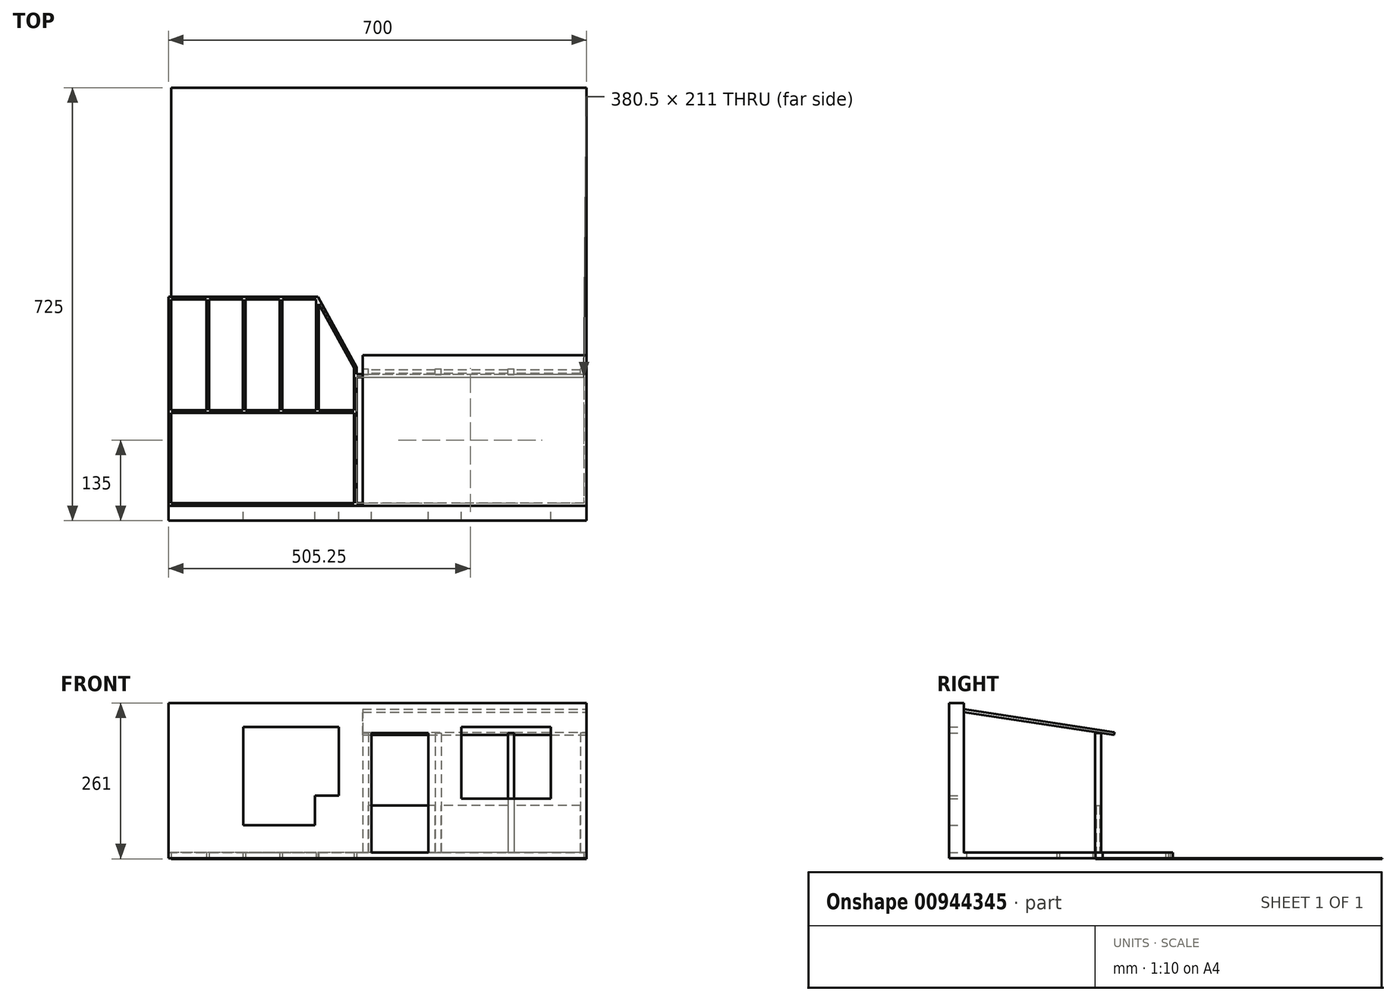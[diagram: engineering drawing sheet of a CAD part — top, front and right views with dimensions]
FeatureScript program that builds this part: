
annotation { "Feature Type Name" : "Feature", "Feature Type Description" : "" }
export const myFeature = defineFeature(function(context is Context, id is Id, definition is map)
    precondition{}
    {
        {
            var Q0;
            Q0=qCreatedBy(makeId("Top.planeOp"),FACE);
            var sketch = newSketch(context, id + "F0", { "sketchPlane" : qUnion([Q0])});
            skLineSegment(sketch, "E0", {"start": v(0, 0) * mm, "end": v(-385, 0) * mm});
            skLineSegment(sketch, "E1", {"start": v(-385, 0) * mm, "end": v(-700, 0) * mm});
            skLineSegment(sketch, "E2", {"start": v(-700, 0) * mm, "end": v(-700, 350) * mm});
            skLineSegment(sketch, "E3", {"start": v(-700, 350) * mm, "end": v(-450, 350) * mm});
            skLineSegment(sketch, "E4", {"start": v(-450, 350) * mm, "end": v(-385, 232) * mm});
            skLineSegment(sketch, "E5", {"start": v(-385, 232) * mm, "end": v(0, 232) * mm, "construction": true});
            skLineSegment(sketch, "E6", {"start": v(0, 232) * mm, "end": v(0, 0) * mm});
            skLineSegment(sketch, "E7", {"start": v(-385, 232) * mm, "end": v(-385, 0) * mm});
            skLineSegment(sketch, "E8", {"start": v(-385, 160) * mm, "end": v(-700, 160) * mm});
            skLineSegment(sketch, "E9", {"start": v(-385, 220) * mm, "end": v(0, 220) * mm});
            skLineSegment(sketch, "E10.0", {"start": v(-389.5, 230.84) * mm, "end": v(-389.5, 0) * mm});
            skLineSegment(sketch, "E10.1", {"start": v(-452.66, 345.5) * mm, "end": v(-389.5, 230.84) * mm});
            skLineSegment(sketch, "E10.2", {"start": v(-695.5, 345.5) * mm, "end": v(-452.66, 345.5) * mm});
            skLineSegment(sketch, "E10.3", {"start": v(-695.5, 0) * mm, "end": v(-695.5, 345.5) * mm});
            skLineSegment(sketch, "E11", {"start": v(-634.3, 160) * mm, "end": v(-634.3, 345.5) * mm, "construction": true});
            skLineSegment(sketch, "E12", {"start": v(-573.1, 160) * mm, "end": v(-573.1, 345.5) * mm, "construction": true});
            skLineSegment(sketch, "E13", {"start": v(-511.9, 160) * mm, "end": v(-511.9, 345.5) * mm, "construction": true});
            skLineSegment(sketch, "E14", {"start": v(-450.7, 160) * mm, "end": v(-450.7, 341.94) * mm, "construction": true});
            skLineSegment(sketch, "E15", {"start": v(-695.5, 257.02) * mm, "end": v(-634.3, 257.02) * mm, "construction": true});
            skLineSegment(sketch, "E16", {"start": v(-634.3, 257.02) * mm, "end": v(-573.1, 257.02) * mm, "construction": true});
            skLineSegment(sketch, "E17", {"start": v(-573.1, 257.02) * mm, "end": v(-511.9, 257.02) * mm, "construction": true});
            skLineSegment(sketch, "E18", {"start": v(-511.9, 257.02) * mm, "end": v(-450.7, 257.02) * mm, "construction": true});
            skLineSegment(sketch, "E19", {"start": v(-450.7, 190.59) * mm, "end": v(-389.5, 190.59) * mm, "construction": true});
            skLineSegment(sketch, "E20.0", {"start": v(-632.05, 160) * mm, "end": v(-632.05, 345.5) * mm});
            skLineSegment(sketch, "E21.0", {"start": v(-636.55, 160) * mm, "end": v(-636.55, 345.5) * mm});
            skLineSegment(sketch, "E22.0", {"start": v(-570.85, 160) * mm, "end": v(-570.85, 345.5) * mm});
            skLineSegment(sketch, "E23.0", {"start": v(-575.35, 160) * mm, "end": v(-575.35, 345.5) * mm});
            skLineSegment(sketch, "E24.0", {"start": v(-509.65, 160) * mm, "end": v(-509.65, 345.5) * mm});
            skLineSegment(sketch, "E25.0", {"start": v(-448.45, 160) * mm, "end": v(-448.45, 341.94) * mm});
            skLineSegment(sketch, "E26.0", {"start": v(-452.95, 160) * mm, "end": v(-452.95, 341.94) * mm});
            skLineSegment(sketch, "E27.0", {"start": v(-514.15, 160) * mm, "end": v(-514.15, 345.5) * mm});
            skLineSegment(sketch, "E28.0", {"start": v(-385, 4.5) * mm, "end": v(-700, 4.5) * mm});
            skLineSegment(sketch, "E28.1", {"start": v(-4.5, 4.5) * mm, "end": v(-385, 4.5) * mm});
            skLineSegment(sketch, "E28.2", {"start": v(-4.5, 232) * mm, "end": v(-4.5, 4.5) * mm});
            skLineSegment(sketch, "E29.0", {"start": v(-385, 215.5) * mm, "end": v(0, 215.5) * mm});
            skLineSegment(sketch, "E30.0", {"start": v(-385, 155.5) * mm, "end": v(-700, 155.5) * mm});
            skLineSegment(sketch, "E31", {"start": v(-452.95, 341.94) * mm, "end": v(-452.66, 347.98) * mm});
            skSolve(sketch);
        }
        {
            var Q0;
            {var subQ0=sQuery(id+"F0.wireOp",EDGE,"E2");var subQ1=sQuery(id+"F0.wireOp",EDGE,"E1");var subQ2=makeQuery(id+"F0.imprint","INTERSECT",VERTEX,{"derivedFrom":[subQ1,subQ0]});Q0=makeQuery(id+"F0.imprint","IMPRINT",FACE,{"disambiguationData":[TD([[makeQuery(id+"F0.imprint","IMPRINT",EDGE,{"disambiguationData":[TD([[subQ2,1.0]])],"derivedFrom":subQ1}),-1.0]])]});}
            var Q1;
            {var subQ0=sQuery(id+"F0.wireOp",EDGE,"E9");var subQ1=sQuery(id+"F0.wireOp",EDGE,"E6");var subQ2=makeQuery(id+"F0.imprint","INTERSECT",VERTEX,{"derivedFrom":[subQ1,subQ0]});Q1=makeQuery(id+"F0.imprint","IMPRINT",FACE,{"disambiguationData":[TD([[makeQuery(id+"F0.imprint","IMPRINT",EDGE,{"disambiguationData":[TD([[subQ2,-1.0]])],"derivedFrom":subQ1}),-1.0]])]});}
            var Q2;
            {var subQ1=sQuery(id+"F0.wireOp",EDGE,"E0");Q2=makeQuery(id+"F0.imprint","IMPRINT",FACE,{"disambiguationData":[TD([[makeQuery(id+"F0.imprint","IMPRINT",EDGE,{"derivedFrom":subQ1}),-1.0]])]});}
            var Q3;
            {var subQ1=sQuery(id+"F0.wireOp",EDGE,"E1");var subQ3=sQuery(id+"F0.wireOp",EDGE,"E10.0");var subQ4=makeQuery(id+"F0.imprint","INTERSECT",VERTEX,{"derivedFrom":[subQ1,subQ3]});Q3=makeQuery(id+"F0.imprint","IMPRINT",FACE,{"disambiguationData":[TD([[makeQuery(id+"F0.imprint","IMPRINT",EDGE,{"disambiguationData":[TD([[subQ4,1.0]])],"derivedFrom":subQ3}),1.0]])]});}
            var Q4;
            {var subQ0=sQuery(id+"F0.wireOp",EDGE,"E10.0");var subQ1=sQuery(id+"F0.wireOp",EDGE,"E1");var subQ2=makeQuery(id+"F0.imprint","INTERSECT",VERTEX,{"derivedFrom":[subQ1,subQ0]});Q4=makeQuery(id+"F0.imprint","IMPRINT",FACE,{"disambiguationData":[TD([[makeQuery(id+"F0.imprint","IMPRINT",EDGE,{"disambiguationData":[TD([[subQ2,-1.0]])],"derivedFrom":subQ1}),-1.0]])]});}
            var Q5;
            {var subQ0=sQuery(id+"F0.wireOp",EDGE,"E28.0");var subQ1=sQuery(id+"F0.wireOp",EDGE,"E2");var subQ2=makeQuery(id+"F0.imprint","INTERSECT",VERTEX,{"derivedFrom":[subQ1,subQ0]});Q5=makeQuery(id+"F0.imprint","IMPRINT",FACE,{"disambiguationData":[TD([[makeQuery(id+"F0.imprint","IMPRINT",EDGE,{"disambiguationData":[TD([[subQ2,-1.0]])],"derivedFrom":subQ1}),-1.0]])]});}
            var Q6;
            {var subQ0=sQuery(id+"F0.wireOp",EDGE,"E8");var subQ1=sQuery(id+"F0.wireOp",EDGE,"E2");var subQ2=makeQuery(id+"F0.imprint","INTERSECT",VERTEX,{"derivedFrom":[subQ1,subQ0]});Q6=makeQuery(id+"F0.imprint","IMPRINT",FACE,{"disambiguationData":[TD([[makeQuery(id+"F0.imprint","IMPRINT",EDGE,{"disambiguationData":[TD([[subQ2,1.0]])],"derivedFrom":subQ1}),-1.0]])]});}
            var Q7;
            {var subQ0=sQuery(id+"F0.wireOp",EDGE,"E9");var subQ1=sQuery(id+"F0.wireOp",EDGE,"E7");var subQ2=makeQuery(id+"F0.imprint","INTERSECT",VERTEX,{"derivedFrom":[subQ1,subQ0]});Q7=makeQuery(id+"F0.imprint","IMPRINT",FACE,{"disambiguationData":[TD([[makeQuery(id+"F0.imprint","IMPRINT",EDGE,{"disambiguationData":[TD([[subQ2,-1.0]])],"derivedFrom":subQ1}),1.0]])]});}
            var Q8;
            {var subQ9=sQuery(id+"F0.wireOp",EDGE,"E26.0");Q8=makeQuery(id+"F0.imprint","IMPRINT",FACE,{"disambiguationData":[TD([[makeQuery(id+"F0.imprint","IMPRINT",EDGE,{"derivedFrom":subQ9}),-1.0]])]});}
            var Q9;
            {var subQ21=sQuery(id+"F0.wireOp",EDGE,"E3");Q9=makeQuery(id+"F0.imprint","IMPRINT",FACE,{"disambiguationData":[TD([[makeQuery(id+"F0.imprint","IMPRINT",EDGE,{"derivedFrom":subQ21}),-1.0]])]});}
            var Q10;
            {var subQ0=sQuery(id+"F0.wireOp",EDGE,"E24.0");Q10=makeQuery(id+"F0.imprint","IMPRINT",FACE,{"disambiguationData":[TD([[makeQuery(id+"F0.imprint","IMPRINT",EDGE,{"derivedFrom":subQ0}),1.0]])]});}
            var Q11;
            {var subQ0=sQuery(id+"F0.wireOp",EDGE,"E22.0");Q11=makeQuery(id+"F0.imprint","IMPRINT",FACE,{"disambiguationData":[TD([[makeQuery(id+"F0.imprint","IMPRINT",EDGE,{"derivedFrom":subQ0}),1.0]])]});}
            var Q12;
            {var subQ0=sQuery(id+"F0.wireOp",EDGE,"E20.0");Q12=makeQuery(id+"F0.imprint","IMPRINT",FACE,{"disambiguationData":[TD([[makeQuery(id+"F0.imprint","IMPRINT",EDGE,{"derivedFrom":subQ0}),1.0]])]});}
            var Q13;
            {var subQ0=sQuery(id+"F0.wireOp",EDGE,"E8");var subQ10=makeQuery(id+"F0.imprint","INTERSECT",VERTEX,{"derivedFrom":[subQ0,sQuery(id+"F0.wireOp",EDGE,"E25.0")]});Q13=makeQuery(id+"F0.imprint","IMPRINT",FACE,{"disambiguationData":[TD([[makeQuery(id+"F0.imprint","IMPRINT",EDGE,{"disambiguationData":[TD([[subQ10,1.0]])],"derivedFrom":subQ0}),1.0]])]});}
            var Q14;
            {var subQ0=sQuery(id+"F0.wireOp",EDGE,"E8");var subQ1=sQuery(id+"F0.wireOp",EDGE,"E7");var subQ2=makeQuery(id+"F0.imprint","INTERSECT",VERTEX,{"derivedFrom":[subQ1,subQ0]});Q14=makeQuery(id+"F0.imprint","IMPRINT",FACE,{"disambiguationData":[TD([[makeQuery(id+"F0.imprint","IMPRINT",EDGE,{"disambiguationData":[TD([[subQ2,-1.0]])],"derivedFrom":subQ1}),-1.0]])]});}
            var Q15;
            {var subQ3=sQuery(id+"F0.wireOp",EDGE,"E30.0");var subQ5=sQuery(id+"F0.wireOp",EDGE,"E10.0");var subQ6=makeQuery(id+"F0.imprint","INTERSECT",VERTEX,{"derivedFrom":[subQ5,subQ3]});Q15=makeQuery(id+"F0.imprint","IMPRINT",FACE,{"disambiguationData":[TD([[makeQuery(id+"F0.imprint","IMPRINT",EDGE,{"disambiguationData":[TD([[subQ6,-1.0]])],"derivedFrom":subQ5}),1.0]])]});}
            extrude(context, id + "F1", {"entities" : qUnion([Q0, Q1, Q2, Q3, Q4, Q5, Q6, Q7, Q8, Q9, Q10, Q11, Q12, Q13, Q14, Q15]), "depth" : 9.5 * mm, "offsetDistance" : 25 * mm});
        }
        {
            var Q0;
            Q0=makeQuery(id+"F1.opExtrude","SWEPT_FACE",FACE,{"disambiguationData":[OSD([sQuery(id+"F0.wireOp",EDGE,"E0"),sQuery(id+"F0.wireOp",EDGE,"E1")])]});
            var sketch = newSketch(context, id + "F2", { "sketchPlane" : qUnion([Q0])});
            skLineSegment(sketch, "E32.bottom", {"start": v(0, 0) * mm, "end": v(-700, 0) * mm});
            skLineSegment(sketch, "E32.top", {"start": v(0, 260) * mm, "end": v(-700, 260) * mm});
            skLineSegment(sketch, "E32.left", {"start": v(0, 0) * mm, "end": v(0, 260) * mm});
            skLineSegment(sketch, "E32.right", {"start": v(-700, 0) * mm, "end": v(-700, 260) * mm});
            skLineSegment(sketch, "E33.bottom", {"start": v(-60, 99.5) * mm, "end": v(-210, 99.5) * mm});
            skLineSegment(sketch, "E33.top", {"start": v(-60, 219.5) * mm, "end": v(-210, 219.5) * mm});
            skLineSegment(sketch, "E33.left", {"start": v(-60, 99.5) * mm, "end": v(-60, 219.5) * mm});
            skLineSegment(sketch, "E33.right", {"start": v(-210, 99.5) * mm, "end": v(-210, 219.5) * mm});
            skLineSegment(sketch, "E34.bottom", {"start": v(-360, 9.5) * mm, "end": v(-265, 9.5) * mm});
            skLineSegment(sketch, "E34.top", {"start": v(-360, 209.5) * mm, "end": v(-265, 209.5) * mm});
            skLineSegment(sketch, "E34.left", {"start": v(-360, 9.5) * mm, "end": v(-360, 209.5) * mm});
            skLineSegment(sketch, "E34.right", {"start": v(-265, 9.5) * mm, "end": v(-265, 209.5) * mm});
            skLineSegment(sketch, "E35.bottom", {"start": v(-415, 220) * mm, "end": v(-455, 220) * mm});
            skLineSegment(sketch, "E35.top", {"start": v(-415, 105) * mm, "end": v(-455, 105) * mm});
            skLineSegment(sketch, "E35.left", {"start": v(-415, 220) * mm, "end": v(-415, 105) * mm});
            skLineSegment(sketch, "E35.right", {"start": v(-455, 220) * mm, "end": v(-455, 105) * mm});
            skLineSegment(sketch, "E36.bottom", {"start": v(-455, 220) * mm, "end": v(-575, 220) * mm});
            skLineSegment(sketch, "E36.top", {"start": v(-455, 55) * mm, "end": v(-575, 55) * mm});
            skLineSegment(sketch, "E36.left", {"start": v(-455, 220) * mm, "end": v(-455, 55) * mm});
            skLineSegment(sketch, "E36.right", {"start": v(-575, 220) * mm, "end": v(-575, 55) * mm});
            skSolve(sketch);
        }
        {
            var Q0;
            {var subQ1=sQuery(id+"F2.wireOp",EDGE,"E32.bottom");Q0=makeQuery(id+"F2.imprint","IMPRINT",FACE,{"disambiguationData":[TD([[makeQuery(id+"F2.imprint","IMPRINT",EDGE,{"derivedFrom":subQ1}),-1.0]])]});}
            var Q1;
            {var subQ1=sQuery(id+"F2.wireOp",EDGE,"E32.top");Q1=makeQuery(id+"F2.imprint","IMPRINT",FACE,{"disambiguationData":[TD([[makeQuery(id+"F2.imprint","IMPRINT",EDGE,{"derivedFrom":subQ1}),1.0]])]});}
            extrude(context, id + "F3", {"entities" : qUnion([Q0, Q1]), "operationType" : NewBodyOperationType.ADD, "depth" : 25 * mm, "offsetDistance" : 25 * mm});
        }
        {
            var Q0;
            Q0=makeQuery(id+"F3.boolean.opBoolean","MERGE",FACE,{"derivedFrom":[makeQuery(id+"F1.opExtrude","CAP_FACE",FACE,{"disambiguationData":[OSD([sQuery(id+"F0.wireOp",EDGE,"E0"),sQuery(id+"F0.wireOp",EDGE,"E1"),sQuery(id+"F0.wireOp",EDGE,"E2"),sQuery(id+"F0.wireOp",EDGE,"E3"),sQuery(id+"F0.wireOp",EDGE,"E4"),sQuery(id+"F0.wireOp",EDGE,"E6"),sQuery(id+"F0.wireOp",EDGE,"E7"),sQuery(id+"F0.wireOp",EDGE,"E8"),sQuery(id+"F0.wireOp",EDGE,"E9"),sQuery(id+"F0.wireOp",EDGE,"E10.0"),sQuery(id+"F0.wireOp",EDGE,"E10.1"),sQuery(id+"F0.wireOp",EDGE,"E10.2"),sQuery(id+"F0.wireOp",EDGE,"E10.3"),sQuery(id+"F0.wireOp",EDGE,"E20.0"),sQuery(id+"F0.wireOp",EDGE,"E21.0"),sQuery(id+"F0.wireOp",EDGE,"E22.0"),sQuery(id+"F0.wireOp",EDGE,"E23.0"),sQuery(id+"F0.wireOp",EDGE,"E24.0"),sQuery(id+"F0.wireOp",EDGE,"E25.0"),sQuery(id+"F0.wireOp",EDGE,"E26.0"),sQuery(id+"F0.wireOp",EDGE,"E27.0"),sQuery(id+"F0.wireOp",EDGE,"E28.0"),sQuery(id+"F0.wireOp",EDGE,"E28.1"),sQuery(id+"F0.wireOp",EDGE,"E28.2"),sQuery(id+"F0.wireOp",EDGE,"E29.0"),sQuery(id+"F0.wireOp",EDGE,"E30.0"),sQuery(id+"F0.wireOp",EDGE,"E31")])],"isStart":true}),makeQuery(id+"F3.opExtrude","SWEPT_FACE",FACE,{"disambiguationData":[OSD([sQuery(id+"F2.wireOp",EDGE,"E32.bottom")])]})]});
            var sketch = newSketch(context, id + "F4", { "sketchPlane" : qUnion([Q0])});
            skLineSegment(sketch, "E37.bottom", {"start": v(0, 0) * mm, "end": v(-695.5, 0) * mm});
            skLineSegment(sketch, "E37.top", {"start": v(0, -700) * mm, "end": v(-695.5, -700) * mm});
            skLineSegment(sketch, "E37.left", {"start": v(0, 0) * mm, "end": v(0, -700) * mm});
            skLineSegment(sketch, "E37.right", {"start": v(-695.5, 0) * mm, "end": v(-695.5, -700) * mm});
            skSolve(sketch);
        }
        {
            var Q0;
            {var subQ3=sQuery(id+"F4.wireOp",EDGE,"E37.top");Q0=makeQuery(id+"F4.imprint","IMPRINT",FACE,{"disambiguationData":[TD([[makeQuery(id+"F4.imprint","IMPRINT",EDGE,{"derivedFrom":subQ3}),-1.0]])]});}
            extrude(context, id + "F5", {"entities" : qUnion([Q0]), "operationType" : NewBodyOperationType.ADD, "depth" : 1 * mm, "offsetDistance" : 25 * mm});
        }
        {
            var Q0;
            Q0=makeQuery(id+"F3.boolean.opBoolean","MERGE",FACE,{"derivedFrom":[makeQuery(id+"F1.opExtrude","CAP_FACE",FACE,{"disambiguationData":[OSD([sQuery(id+"F0.wireOp",EDGE,"E0"),sQuery(id+"F0.wireOp",EDGE,"E1"),sQuery(id+"F0.wireOp",EDGE,"E2"),sQuery(id+"F0.wireOp",EDGE,"E3"),sQuery(id+"F0.wireOp",EDGE,"E4"),sQuery(id+"F0.wireOp",EDGE,"E6"),sQuery(id+"F0.wireOp",EDGE,"E7"),sQuery(id+"F0.wireOp",EDGE,"E8"),sQuery(id+"F0.wireOp",EDGE,"E9"),sQuery(id+"F0.wireOp",EDGE,"E10.0"),sQuery(id+"F0.wireOp",EDGE,"E10.1"),sQuery(id+"F0.wireOp",EDGE,"E10.2"),sQuery(id+"F0.wireOp",EDGE,"E10.3"),sQuery(id+"F0.wireOp",EDGE,"E20.0"),sQuery(id+"F0.wireOp",EDGE,"E21.0"),sQuery(id+"F0.wireOp",EDGE,"E22.0"),sQuery(id+"F0.wireOp",EDGE,"E23.0"),sQuery(id+"F0.wireOp",EDGE,"E24.0"),sQuery(id+"F0.wireOp",EDGE,"E25.0"),sQuery(id+"F0.wireOp",EDGE,"E26.0"),sQuery(id+"F0.wireOp",EDGE,"E27.0"),sQuery(id+"F0.wireOp",EDGE,"E28.0"),sQuery(id+"F0.wireOp",EDGE,"E28.1"),sQuery(id+"F0.wireOp",EDGE,"E28.2"),sQuery(id+"F0.wireOp",EDGE,"E29.0"),sQuery(id+"F0.wireOp",EDGE,"E30.0"),sQuery(id+"F0.wireOp",EDGE,"E31")])],"isStart":false}),makeQuery(id+"F3.opExtrude","SWEPT_FACE",FACE,{"disambiguationData":[OSD([sQuery(id+"F2.wireOp",EDGE,"E34.bottom")])]})]});
            var sketch = newSketch(context, id + "F6", { "sketchPlane" : qUnion([Q0])});
            skLineSegment(sketch, "E38.bottom", {"start": v(0, 0.5) * mm, "end": v(-700, 0.5) * mm});
            skLineSegment(sketch, "E38.top", {"start": v(0, 15) * mm, "end": v(-700, 15) * mm});
            skLineSegment(sketch, "E38.left", {"start": v(0, 0.5) * mm, "end": v(0, 15) * mm});
            skLineSegment(sketch, "E38.right", {"start": v(-700, 0.5) * mm, "end": v(-700, 15) * mm});
            skLineSegment(sketch, "E39.0.1.0", {"start": v(0, 29.6) * mm, "end": v(-700, 29.6) * mm});
            skLineSegment(sketch, "E39.0.1.1", {"start": v(0, 15.1) * mm, "end": v(-700, 15.1) * mm});
            skLineSegment(sketch, "E39.0.1.2", {"start": v(-700, 15.1) * mm, "end": v(-700, 29.6) * mm});
            skLineSegment(sketch, "E39.0.1.3", {"start": v(0, 15.1) * mm, "end": v(0, 29.6) * mm});
            skLineSegment(sketch, "E39.0.2.0", {"start": v(0, 44.2) * mm, "end": v(-700, 44.2) * mm});
            skLineSegment(sketch, "E39.0.2.1", {"start": v(0, 29.7) * mm, "end": v(-700, 29.7) * mm});
            skLineSegment(sketch, "E39.0.2.2", {"start": v(-700, 29.7) * mm, "end": v(-700, 44.2) * mm});
            skLineSegment(sketch, "E39.0.2.3", {"start": v(0, 29.7) * mm, "end": v(0, 44.2) * mm});
            skLineSegment(sketch, "E39.0.3.0", {"start": v(0, 58.8) * mm, "end": v(-700, 58.8) * mm});
            skLineSegment(sketch, "E39.0.3.1", {"start": v(0, 44.3) * mm, "end": v(-700, 44.3) * mm});
            skLineSegment(sketch, "E39.0.3.2", {"start": v(-700, 44.3) * mm, "end": v(-700, 58.8) * mm});
            skLineSegment(sketch, "E39.0.3.3", {"start": v(0, 44.3) * mm, "end": v(0, 58.8) * mm});
            skLineSegment(sketch, "E39.0.4.0", {"start": v(0, 73.4) * mm, "end": v(-700, 73.4) * mm});
            skLineSegment(sketch, "E39.0.4.1", {"start": v(0, 58.9) * mm, "end": v(-700, 58.9) * mm});
            skLineSegment(sketch, "E39.0.4.2", {"start": v(-700, 58.9) * mm, "end": v(-700, 73.4) * mm});
            skLineSegment(sketch, "E39.0.4.3", {"start": v(0, 58.9) * mm, "end": v(0, 73.4) * mm});
            skLineSegment(sketch, "E39.0.5.0", {"start": v(0, 88) * mm, "end": v(-700, 88) * mm});
            skLineSegment(sketch, "E39.0.5.1", {"start": v(0, 73.5) * mm, "end": v(-700, 73.5) * mm});
            skLineSegment(sketch, "E39.0.5.2", {"start": v(-700, 73.5) * mm, "end": v(-700, 88) * mm});
            skLineSegment(sketch, "E39.0.5.3", {"start": v(0, 73.5) * mm, "end": v(0, 88) * mm});
            skLineSegment(sketch, "E39.0.6.0", {"start": v(0, 102.6) * mm, "end": v(-700, 102.6) * mm});
            skLineSegment(sketch, "E39.0.6.1", {"start": v(0, 88.1) * mm, "end": v(-700, 88.1) * mm});
            skLineSegment(sketch, "E39.0.6.2", {"start": v(-700, 88.1) * mm, "end": v(-700, 102.6) * mm});
            skLineSegment(sketch, "E39.0.6.3", {"start": v(0, 88.1) * mm, "end": v(0, 102.6) * mm});
            skLineSegment(sketch, "E39.0.7.0", {"start": v(0, 117.2) * mm, "end": v(-700, 117.2) * mm});
            skLineSegment(sketch, "E39.0.7.1", {"start": v(0, 102.7) * mm, "end": v(-700, 102.7) * mm});
            skLineSegment(sketch, "E39.0.7.2", {"start": v(-700, 102.7) * mm, "end": v(-700, 117.2) * mm});
            skLineSegment(sketch, "E39.0.7.3", {"start": v(0, 102.7) * mm, "end": v(0, 117.2) * mm});
            skLineSegment(sketch, "E39.0.8.0", {"start": v(0, 131.8) * mm, "end": v(-700, 131.8) * mm});
            skLineSegment(sketch, "E39.0.8.1", {"start": v(0, 117.3) * mm, "end": v(-700, 117.3) * mm});
            skLineSegment(sketch, "E39.0.8.2", {"start": v(-700, 117.3) * mm, "end": v(-700, 131.8) * mm});
            skLineSegment(sketch, "E39.0.8.3", {"start": v(0, 117.3) * mm, "end": v(0, 131.8) * mm});
            skLineSegment(sketch, "E39.0.9.0", {"start": v(0, 146.4) * mm, "end": v(-700, 146.4) * mm});
            skLineSegment(sketch, "E39.0.9.1", {"start": v(0, 131.9) * mm, "end": v(-700, 131.9) * mm});
            skLineSegment(sketch, "E39.0.9.2", {"start": v(-700, 131.9) * mm, "end": v(-700, 146.4) * mm});
            skLineSegment(sketch, "E39.0.9.3", {"start": v(0, 131.9) * mm, "end": v(0, 146.4) * mm});
            skLineSegment(sketch, "E39.0.10.0", {"start": v(0, 161) * mm, "end": v(-700, 161) * mm});
            skLineSegment(sketch, "E39.0.10.1", {"start": v(0, 146.5) * mm, "end": v(-700, 146.5) * mm});
            skLineSegment(sketch, "E39.0.10.2", {"start": v(-700, 146.5) * mm, "end": v(-700, 161) * mm});
            skLineSegment(sketch, "E39.0.10.3", {"start": v(0, 146.5) * mm, "end": v(0, 161) * mm});
            skLineSegment(sketch, "E39.0.11.0", {"start": v(0, 175.6) * mm, "end": v(-700, 175.6) * mm});
            skLineSegment(sketch, "E39.0.11.1", {"start": v(0, 161.1) * mm, "end": v(-700, 161.1) * mm});
            skLineSegment(sketch, "E39.0.11.2", {"start": v(-700, 161.1) * mm, "end": v(-700, 175.6) * mm});
            skLineSegment(sketch, "E39.0.11.3", {"start": v(0, 161.1) * mm, "end": v(0, 175.6) * mm});
            skLineSegment(sketch, "E39.0.12.0", {"start": v(0, 190.2) * mm, "end": v(-700, 190.2) * mm});
            skLineSegment(sketch, "E39.0.12.1", {"start": v(0, 175.7) * mm, "end": v(-700, 175.7) * mm});
            skLineSegment(sketch, "E39.0.12.2", {"start": v(-700, 175.7) * mm, "end": v(-700, 190.2) * mm});
            skLineSegment(sketch, "E39.0.12.3", {"start": v(0, 175.7) * mm, "end": v(0, 190.2) * mm});
            skLineSegment(sketch, "E39.0.13.0", {"start": v(0, 204.8) * mm, "end": v(-700, 204.8) * mm});
            skLineSegment(sketch, "E39.0.13.1", {"start": v(0, 190.3) * mm, "end": v(-700, 190.3) * mm});
            skLineSegment(sketch, "E39.0.13.2", {"start": v(-700, 190.3) * mm, "end": v(-700, 204.8) * mm});
            skLineSegment(sketch, "E39.0.13.3", {"start": v(0, 190.3) * mm, "end": v(0, 204.8) * mm});
            skLineSegment(sketch, "E39.0.14.0", {"start": v(0, 219.4) * mm, "end": v(-700, 219.4) * mm});
            skLineSegment(sketch, "E39.0.14.1", {"start": v(0, 204.9) * mm, "end": v(-700, 204.9) * mm});
            skLineSegment(sketch, "E39.0.14.2", {"start": v(-700, 204.9) * mm, "end": v(-700, 219.4) * mm});
            skLineSegment(sketch, "E39.0.14.3", {"start": v(0, 204.9) * mm, "end": v(0, 219.4) * mm});
            skLineSegment(sketch, "E39.0.15.0", {"start": v(0, 234) * mm, "end": v(-700, 234) * mm});
            skLineSegment(sketch, "E39.0.15.1", {"start": v(0, 219.5) * mm, "end": v(-700, 219.5) * mm});
            skLineSegment(sketch, "E39.0.15.2", {"start": v(-700, 219.5) * mm, "end": v(-700, 234) * mm});
            skLineSegment(sketch, "E39.0.15.3", {"start": v(0, 219.5) * mm, "end": v(0, 234) * mm});
            skLineSegment(sketch, "E39.0.16.0", {"start": v(0, 248.6) * mm, "end": v(-700, 248.6) * mm});
            skLineSegment(sketch, "E39.0.16.1", {"start": v(0, 234.1) * mm, "end": v(-700, 234.1) * mm});
            skLineSegment(sketch, "E39.0.16.2", {"start": v(-700, 234.1) * mm, "end": v(-700, 248.6) * mm});
            skLineSegment(sketch, "E39.0.16.3", {"start": v(0, 234.1) * mm, "end": v(0, 248.6) * mm});
            skLineSegment(sketch, "E39.0.17.0", {"start": v(0, 263.2) * mm, "end": v(-700, 263.2) * mm});
            skLineSegment(sketch, "E39.0.17.1", {"start": v(0, 248.7) * mm, "end": v(-700, 248.7) * mm});
            skLineSegment(sketch, "E39.0.17.2", {"start": v(-700, 248.7) * mm, "end": v(-700, 263.2) * mm});
            skLineSegment(sketch, "E39.0.17.3", {"start": v(0, 248.7) * mm, "end": v(0, 263.2) * mm});
            skLineSegment(sketch, "E39.0.18.0", {"start": v(0, 277.8) * mm, "end": v(-700, 277.8) * mm});
            skLineSegment(sketch, "E39.0.18.1", {"start": v(0, 263.3) * mm, "end": v(-700, 263.3) * mm});
            skLineSegment(sketch, "E39.0.18.2", {"start": v(-700, 263.3) * mm, "end": v(-700, 277.8) * mm});
            skLineSegment(sketch, "E39.0.18.3", {"start": v(0, 263.3) * mm, "end": v(0, 277.8) * mm});
            skLineSegment(sketch, "E39.0.19.0", {"start": v(0, 292.4) * mm, "end": v(-700, 292.4) * mm});
            skLineSegment(sketch, "E39.0.19.1", {"start": v(0, 277.9) * mm, "end": v(-700, 277.9) * mm});
            skLineSegment(sketch, "E39.0.19.2", {"start": v(-700, 277.9) * mm, "end": v(-700, 292.4) * mm});
            skLineSegment(sketch, "E39.0.19.3", {"start": v(0, 277.9) * mm, "end": v(0, 292.4) * mm});
            skLineSegment(sketch, "E39.0.20.0", {"start": v(0, 307) * mm, "end": v(-700, 307) * mm});
            skLineSegment(sketch, "E39.0.20.1", {"start": v(0, 292.5) * mm, "end": v(-700, 292.5) * mm});
            skLineSegment(sketch, "E39.0.20.2", {"start": v(-700, 292.5) * mm, "end": v(-700, 307) * mm});
            skLineSegment(sketch, "E39.0.20.3", {"start": v(0, 292.5) * mm, "end": v(0, 307) * mm});
            skLineSegment(sketch, "E39.0.21.0", {"start": v(0, 321.6) * mm, "end": v(-700, 321.6) * mm});
            skLineSegment(sketch, "E39.0.21.1", {"start": v(0, 307.1) * mm, "end": v(-700, 307.1) * mm});
            skLineSegment(sketch, "E39.0.21.2", {"start": v(-700, 307.1) * mm, "end": v(-700, 321.6) * mm});
            skLineSegment(sketch, "E39.0.21.3", {"start": v(0, 307.1) * mm, "end": v(0, 321.6) * mm});
            skLineSegment(sketch, "E39.0.22.0", {"start": v(0, 336.2) * mm, "end": v(-700, 336.2) * mm});
            skLineSegment(sketch, "E39.0.22.1", {"start": v(0, 321.7) * mm, "end": v(-700, 321.7) * mm});
            skLineSegment(sketch, "E39.0.22.2", {"start": v(-700, 321.7) * mm, "end": v(-700, 336.2) * mm});
            skLineSegment(sketch, "E39.0.22.3", {"start": v(0, 321.7) * mm, "end": v(0, 336.2) * mm});
            skLineSegment(sketch, "E39.direction1", {"start": v(-700, 15) * mm, "end": v(-675, 15) * mm, "construction": true});
            skLineSegment(sketch, "E39.direction2", {"start": v(-700, 15) * mm, "end": v(-700, 29.6) * mm, "construction": true});
            skLineSegment(sketch, "E40.0.0.23", {"start": v(0, 350.8) * mm, "end": v(-700, 350.8) * mm});
            skLineSegment(sketch, "E40.3.0.23", {"start": v(0, 336.3) * mm, "end": v(-700, 336.3) * mm});
            skLineSegment(sketch, "E40.6.0.23", {"start": v(-700, 336.3) * mm, "end": v(-700, 350.8) * mm});
            skLineSegment(sketch, "E40.9.0.23", {"start": v(0, 336.3) * mm, "end": v(0, 350.8) * mm});
            skSolve(sketch);
        }
        {
            var Q0;
            Q0=makeQuery(id+"F5.opExtrude","CAP_FACE",FACE,{"disambiguationData":[OSD([sQuery(id+"F0.wireOp",EDGE,"E3"),sQuery(id+"F0.wireOp",EDGE,"E4"),sQuery(id+"F0.wireOp",EDGE,"E7"),sQuery(id+"F0.wireOp",EDGE,"E9"),sQuery(id+"F4.wireOp",EDGE,"E37.top"),sQuery(id+"F4.wireOp",EDGE,"E37.left"),sQuery(id+"F4.wireOp",EDGE,"E37.right")])],"isStart":true});
            var sketch = newSketch(context, id + "F7", { "sketchPlane" : qUnion([Q0])});
            skLineSegment(sketch, "E41.0.0", {"start": v(-450, 350) * mm, "end": v(-695.5, 350) * mm});
            skLineSegment(sketch, "E41.0.1", {"start": v(-695.5, 350) * mm, "end": v(-695.5, 700) * mm});
            skLineSegment(sketch, "E41.0.2", {"start": v(-695.5, 700) * mm, "end": v(0, 700) * mm});
            skLineSegment(sketch, "E41.0.3", {"start": v(0, 700) * mm, "end": v(0, 220) * mm});
            skLineSegment(sketch, "E41.0.4", {"start": v(0, 220) * mm, "end": v(-385, 220) * mm});
            skLineSegment(sketch, "E41.0.5", {"start": v(-385, 220) * mm, "end": v(-385, 232) * mm});
            skLineSegment(sketch, "E41.0.6", {"start": v(-385, 232) * mm, "end": v(-450, 350) * mm});
            skSolve(sketch);
        }
        {
            var Q0;
            Q0 = qSketchRegion(id + "F7", true);
            extrude(context, id + "F8", {"entities" : qUnion([Q0]), "operationType" : NewBodyOperationType.REMOVE, "endBound" : BoundingType.THROUGH_ALL, "depth" : 25 * mm, "offsetDistance" : 25 * mm});
        }
        {
            var Q0;
            {var subQ0=sQuery(id+"F0.wireOp",EDGE,"E6");var subQ1=sQuery(id+"F0.wireOp",EDGE,"E28.2");var subQ2=sQuery(id+"F6.wireOp",EDGE,"E39.0.14.1");var subQ3=sQuery(id+"F6.wireOp",EDGE,"E39.0.13.0");var subQ4=sQuery(id+"F6.wireOp",EDGE,"E39.0.13.3");var subQ5=sQuery(id+"F6.wireOp",EDGE,"E39.0.14.3");Q0=makeQuery(id+"FQyzF96Mlg0WZgH_2.boolean.opBoolean","SPLIT",FACE,{"disambiguationData":[TD([makeQuery(id+"F1.opExtrude","SWEPT_FACE",FACE,{"disambiguationData":[OSD([subQ0])]}),makeQuery(id+"F1.opExtrude","SWEPT_FACE",FACE,{"disambiguationData":[OSD([subQ1])]}),makeQuery(id+"F3.opExtrude","SWEPT_FACE",FACE,{"disambiguationData":[OSD([sQuery(id+"F2.wireOp",EDGE,"E32.left")])]}),makeQuery(id+"FQyzF96Mlg0WZgH_2.opExtrude","SWEPT_FACE",FACE,{"disambiguationData":[OSD([sQuery(id+"F6.wireOp",EDGE,"E38.left")])]}),makeQuery(id+"FQyzF96Mlg0WZgH_2.opExtrude","SWEPT_FACE",FACE,{"disambiguationData":[OSD([sQuery(id+"F6.wireOp",EDGE,"E39.0.1.3")])]}),makeQuery(id+"FQyzF96Mlg0WZgH_2.opExtrude","SWEPT_FACE",FACE,{"disambiguationData":[OSD([sQuery(id+"F6.wireOp",EDGE,"E39.0.2.3")])]}),makeQuery(id+"FQyzF96Mlg0WZgH_2.opExtrude","SWEPT_FACE",FACE,{"disambiguationData":[OSD([sQuery(id+"F6.wireOp",EDGE,"E39.0.3.3")])]}),makeQuery(id+"FQyzF96Mlg0WZgH_2.opExtrude","SWEPT_FACE",FACE,{"disambiguationData":[OSD([sQuery(id+"F6.wireOp",EDGE,"E39.0.4.3")])]}),makeQuery(id+"FQyzF96Mlg0WZgH_2.opExtrude","SWEPT_FACE",FACE,{"disambiguationData":[OSD([sQuery(id+"F6.wireOp",EDGE,"E39.0.5.3")])]}),makeQuery(id+"FQyzF96Mlg0WZgH_2.opExtrude","SWEPT_FACE",FACE,{"disambiguationData":[OSD([sQuery(id+"F6.wireOp",EDGE,"E39.0.6.3")])]}),makeQuery(id+"FQyzF96Mlg0WZgH_2.opExtrude","SWEPT_FACE",FACE,{"disambiguationData":[OSD([sQuery(id+"F6.wireOp",EDGE,"E39.0.7.3")])]}),makeQuery(id+"FQyzF96Mlg0WZgH_2.opExtrude","SWEPT_FACE",FACE,{"disambiguationData":[OSD([sQuery(id+"F6.wireOp",EDGE,"E39.0.8.3")])]}),makeQuery(id+"FQyzF96Mlg0WZgH_2.opExtrude","SWEPT_FACE",FACE,{"disambiguationData":[OSD([sQuery(id+"F6.wireOp",EDGE,"E39.0.9.3")])]}),makeQuery(id+"FQyzF96Mlg0WZgH_2.opExtrude","SWEPT_FACE",FACE,{"disambiguationData":[OSD([sQuery(id+"F6.wireOp",EDGE,"E39.0.10.3")])]}),makeQuery(id+"FQyzF96Mlg0WZgH_2.opExtrude","SWEPT_FACE",FACE,{"disambiguationData":[OSD([sQuery(id+"F6.wireOp",EDGE,"E39.0.11.3")])]}),makeQuery(id+"FQyzF96Mlg0WZgH_2.opExtrude","SWEPT_FACE",FACE,{"disambiguationData":[OSD([sQuery(id+"F6.wireOp",EDGE,"E39.0.12.3")])]}),makeQuery(id+"FQyzF96Mlg0WZgH_2.opExtrude","SWEPT_FACE",FACE,{"disambiguationData":[OSD([subQ3])]}),makeQuery(id+"FQyzF96Mlg0WZgH_2.opExtrude","CAP_FACE",FACE,{"disambiguationData":[OSD([subQ3,sQuery(id+"F6.wireOp",EDGE,"E39.0.13.1"),sQuery(id+"F6.wireOp",EDGE,"E39.0.13.2"),subQ4])],"isStart":true}),makeQuery(id+"FQyzF96Mlg0WZgH_2.opExtrude","SWEPT_FACE",FACE,{"disambiguationData":[OSD([subQ4])]}),makeQuery(id+"FQyzF96Mlg0WZgH_2.opExtrude","CAP_FACE",FACE,{"disambiguationData":[OSD([sQuery(id+"F6.wireOp",EDGE,"E39.0.14.0"),subQ2,sQuery(id+"F6.wireOp",EDGE,"E39.0.14.2"),subQ5])],"isStart":true}),makeQuery(id+"FQyzF96Mlg0WZgH_2.opExtrude","SWEPT_FACE",FACE,{"disambiguationData":[OSD([subQ2])]}),makeQuery(id+"FQyzF96Mlg0WZgH_2.opExtrude","SWEPT_FACE",FACE,{"disambiguationData":[OSD([subQ5])]})])],"derivedFrom":makeQuery(id+"F3.boolean.opBoolean","MERGE",FACE,{"derivedFrom":[makeQuery(id+"F1.opExtrude","CAP_FACE",FACE,{"disambiguationData":[OSD([sQuery(id+"F0.wireOp",EDGE,"E0"),sQuery(id+"F0.wireOp",EDGE,"E1"),sQuery(id+"F0.wireOp",EDGE,"E2"),sQuery(id+"F0.wireOp",EDGE,"E3"),sQuery(id+"F0.wireOp",EDGE,"E4"),subQ0,sQuery(id+"F0.wireOp",EDGE,"E7"),sQuery(id+"F0.wireOp",EDGE,"E8"),sQuery(id+"F0.wireOp",EDGE,"E9"),sQuery(id+"F0.wireOp",EDGE,"E10.0"),sQuery(id+"F0.wireOp",EDGE,"E10.1"),sQuery(id+"F0.wireOp",EDGE,"E10.2"),sQuery(id+"F0.wireOp",EDGE,"E10.3"),sQuery(id+"F0.wireOp",EDGE,"E20.0"),sQuery(id+"F0.wireOp",EDGE,"E21.0"),sQuery(id+"F0.wireOp",EDGE,"E22.0"),sQuery(id+"F0.wireOp",EDGE,"E23.0"),sQuery(id+"F0.wireOp",EDGE,"E24.0"),sQuery(id+"F0.wireOp",EDGE,"E25.0"),sQuery(id+"F0.wireOp",EDGE,"E26.0"),sQuery(id+"F0.wireOp",EDGE,"E27.0"),sQuery(id+"F0.wireOp",EDGE,"E28.0"),sQuery(id+"F0.wireOp",EDGE,"E28.1"),subQ1,sQuery(id+"F0.wireOp",EDGE,"E29.0"),sQuery(id+"F0.wireOp",EDGE,"E30.0"),sQuery(id+"F0.wireOp",EDGE,"E31")])],"isStart":false}),makeQuery(id+"F3.opExtrude","SWEPT_FACE",FACE,{"disambiguationData":[OSD([sQuery(id+"F2.wireOp",EDGE,"E34.bottom")])]})]})});}
            var sketch = newSketch(context, id + "F9", { "sketchPlane" : qUnion([Q0])});
            skLineSegment(sketch, "E42.bottom", {"start": v(0, 219.49) * mm, "end": v(-10, 219.49) * mm});
            skLineSegment(sketch, "E42.top", {"start": v(0, 229.49) * mm, "end": v(-10, 229.49) * mm});
            skLineSegment(sketch, "E42.left", {"start": v(0, 219.49) * mm, "end": v(0, 229.49) * mm});
            skLineSegment(sketch, "E42.right", {"start": v(-10, 219.49) * mm, "end": v(-10, 229.49) * mm});
            skLineSegment(sketch, "E43.bottom", {"start": v(-375, 219.49) * mm, "end": v(-365, 219.49) * mm});
            skLineSegment(sketch, "E43.top", {"start": v(-375, 229.49) * mm, "end": v(-365, 229.49) * mm});
            skLineSegment(sketch, "E43.left", {"start": v(-375, 219.49) * mm, "end": v(-375, 229.49) * mm});
            skLineSegment(sketch, "E43.right", {"start": v(-365, 219.49) * mm, "end": v(-365, 229.49) * mm});
            skLineSegment(sketch, "E44.bottom", {"start": v(-253.33, 219.49) * mm, "end": v(-243.33, 219.49) * mm});
            skLineSegment(sketch, "E44.top", {"start": v(-253.33, 229.49) * mm, "end": v(-243.33, 229.49) * mm});
            skLineSegment(sketch, "E44.left", {"start": v(-253.33, 219.49) * mm, "end": v(-253.33, 229.49) * mm});
            skLineSegment(sketch, "E44.right", {"start": v(-243.33, 219.49) * mm, "end": v(-243.33, 229.49) * mm});
            skLineSegment(sketch, "E45.bottom", {"start": v(-131.67, 219.49) * mm, "end": v(-121.67, 219.49) * mm});
            skLineSegment(sketch, "E45.top", {"start": v(-131.67, 229.49) * mm, "end": v(-121.67, 229.49) * mm});
            skLineSegment(sketch, "E45.left", {"start": v(-131.67, 219.49) * mm, "end": v(-131.67, 229.49) * mm});
            skLineSegment(sketch, "E45.right", {"start": v(-121.67, 219.49) * mm, "end": v(-121.67, 229.49) * mm});
            skLineSegment(sketch, "E46", {"start": v(-10, 229.49) * mm, "end": v(-121.67, 229.49) * mm, "construction": true});
            skLineSegment(sketch, "E47", {"start": v(-131.67, 229.49) * mm, "end": v(-243.33, 229.49) * mm, "construction": true});
            skLineSegment(sketch, "E48", {"start": v(-253.33, 229.49) * mm, "end": v(-365, 229.49) * mm, "construction": true});
            skSolve(sketch);
        }
        {
            var Q0;
            Q0 = qSketchRegion(id + "F9", true);
            extrude(context, id + "F10", {"entities" : qUnion([Q0]), "operationType" : NewBodyOperationType.ADD, "depth" : 200 * mm, "offsetDistance" : 25 * mm});
        }
        {
            var Q0;
            Q0=makeQuery(id+"F10.boolean.opBoolean","MERGE",FACE,{"derivedFrom":[makeQuery(id+"FQyzF96Mlg0WZgH_2.boolean.opBoolean","MERGE",FACE,{"derivedFrom":[makeQuery(id+"F3.boolean.opBoolean","MERGE",FACE,{"derivedFrom":[makeQuery(id+"F1.opExtrude","SWEPT_FACE",FACE,{"disambiguationData":[OSD([sQuery(id+"F0.wireOp",EDGE,"E6")])]}),makeQuery(id+"F3.opExtrude","SWEPT_FACE",FACE,{"disambiguationData":[OSD([sQuery(id+"F2.wireOp",EDGE,"E32.left")])]})]}),makeQuery(id+"FQyzF96Mlg0WZgH_2.opExtrude","SWEPT_FACE",FACE,{"disambiguationData":[OSD([sQuery(id+"F6.wireOp",EDGE,"E38.left")])]}),makeQuery(id+"FQyzF96Mlg0WZgH_2.opExtrude","SWEPT_FACE",FACE,{"disambiguationData":[OSD([sQuery(id+"F6.wireOp",EDGE,"E39.0.1.3")])]}),makeQuery(id+"FQyzF96Mlg0WZgH_2.opExtrude","SWEPT_FACE",FACE,{"disambiguationData":[OSD([sQuery(id+"F6.wireOp",EDGE,"E39.0.2.3")])]}),makeQuery(id+"FQyzF96Mlg0WZgH_2.opExtrude","SWEPT_FACE",FACE,{"disambiguationData":[OSD([sQuery(id+"F6.wireOp",EDGE,"E39.0.3.3")])]}),makeQuery(id+"FQyzF96Mlg0WZgH_2.opExtrude","SWEPT_FACE",FACE,{"disambiguationData":[OSD([sQuery(id+"F6.wireOp",EDGE,"E39.0.4.3")])]}),makeQuery(id+"FQyzF96Mlg0WZgH_2.opExtrude","SWEPT_FACE",FACE,{"disambiguationData":[OSD([sQuery(id+"F6.wireOp",EDGE,"E39.0.5.3")])]}),makeQuery(id+"FQyzF96Mlg0WZgH_2.opExtrude","SWEPT_FACE",FACE,{"disambiguationData":[OSD([sQuery(id+"F6.wireOp",EDGE,"E39.0.6.3")])]}),makeQuery(id+"FQyzF96Mlg0WZgH_2.opExtrude","SWEPT_FACE",FACE,{"disambiguationData":[OSD([sQuery(id+"F6.wireOp",EDGE,"E39.0.7.3")])]}),makeQuery(id+"FQyzF96Mlg0WZgH_2.opExtrude","SWEPT_FACE",FACE,{"disambiguationData":[OSD([sQuery(id+"F6.wireOp",EDGE,"E39.0.8.3")])]}),makeQuery(id+"FQyzF96Mlg0WZgH_2.opExtrude","SWEPT_FACE",FACE,{"disambiguationData":[OSD([sQuery(id+"F6.wireOp",EDGE,"E39.0.9.3")])]}),makeQuery(id+"FQyzF96Mlg0WZgH_2.opExtrude","SWEPT_FACE",FACE,{"disambiguationData":[OSD([sQuery(id+"F6.wireOp",EDGE,"E39.0.10.3")])]}),makeQuery(id+"FQyzF96Mlg0WZgH_2.opExtrude","SWEPT_FACE",FACE,{"disambiguationData":[OSD([sQuery(id+"F6.wireOp",EDGE,"E39.0.11.3")])]}),makeQuery(id+"FQyzF96Mlg0WZgH_2.opExtrude","SWEPT_FACE",FACE,{"disambiguationData":[OSD([sQuery(id+"F6.wireOp",EDGE,"E39.0.12.3")])]}),makeQuery(id+"FQyzF96Mlg0WZgH_2.opExtrude","SWEPT_FACE",FACE,{"disambiguationData":[OSD([sQuery(id+"F6.wireOp",EDGE,"E39.0.13.3")])]}),makeQuery(id+"FQyzF96Mlg0WZgH_2.opExtrude","SWEPT_FACE",FACE,{"disambiguationData":[OSD([sQuery(id+"F6.wireOp",EDGE,"E39.0.14.3")])]})]}),makeQuery(id+"F10.opExtrude","SWEPT_FACE",FACE,{"disambiguationData":[OSD([sQuery(id+"F9.wireOp",EDGE,"E42.left")])]})]});
            var sketch = newSketch(context, id + "F11", { "sketchPlane" : qUnion([Q0])});
            skLineSegment(sketch, "E49", {"start": v(252.06, 211.12) * mm, "end": v(251.3, 206.17) * mm});
            skLineSegment(sketch, "E50", {"start": v(251.3, 206.17) * mm, "end": v(0, 244.5) * mm});
            skLineSegment(sketch, "E51", {"start": v(0, 244.5) * mm, "end": v(0, 249.56) * mm});
            skLineSegment(sketch, "E52", {"start": v(0, 249.56) * mm, "end": v(252.06, 211.12) * mm});
            skSolve(sketch);
        }
        {
            var Q0;
            {var subQ4=sQuery(id+"F11.wireOp",EDGE,"E49");Q0=makeQuery(id+"F11.imprint","IMPRINT",FACE,{"disambiguationData":[TD([[makeQuery(id+"F11.imprint","IMPRINT",EDGE,{"derivedFrom":subQ4}),-1.0]])]});}
            var Q1;
            Q1=makeQuery(id+"F10.opExtrude","SWEPT_FACE",FACE,{"disambiguationData":[OSD([sQuery(id+"F9.wireOp",EDGE,"E43.left")])]});
            extrude(context, id + "F12", {"entities" : qUnion([Q0]), "endBound" : BoundingType.UP_TO_SURFACE, "oppositeDirection" : true, "depth" : 25 * mm, "endBoundEntityFace" : qUnion([Q1]), "offsetDistance" : 25 * mm});
        }
        {
            var Q0;
            Q0=makeQuery(id+"F10.opExtrude","SWEPT_FACE",FACE,{"disambiguationData":[OSD([sQuery(id+"F9.wireOp",EDGE,"E45.top")])]});
            var sketch = newSketch(context, id + "F13", { "sketchPlane" : qUnion([Q0])});
            skLineSegment(sketch, "E53.bottom", {"start": v(10, 9.5) * mm, "end": v(121.67, 9.5) * mm});
            skLineSegment(sketch, "E53.top", {"start": v(10, 88.21) * mm, "end": v(121.67, 88.21) * mm});
            skLineSegment(sketch, "E53.left", {"start": v(10, 9.5) * mm, "end": v(10, 88.21) * mm});
            skLineSegment(sketch, "E53.right", {"start": v(121.67, 9.5) * mm, "end": v(121.67, 88.21) * mm});
            skLineSegment(sketch, "E54.bottom", {"start": v(131.67, 9.5) * mm, "end": v(243.33, 9.5) * mm});
            skLineSegment(sketch, "E54.top", {"start": v(131.67, 88.21) * mm, "end": v(243.33, 88.21) * mm});
            skLineSegment(sketch, "E54.left", {"start": v(131.67, 9.5) * mm, "end": v(131.67, 88.21) * mm});
            skLineSegment(sketch, "E54.right", {"start": v(243.33, 9.5) * mm, "end": v(243.33, 88.21) * mm});
            skLineSegment(sketch, "E55.bottom", {"start": v(253.33, 9.5) * mm, "end": v(365, 9.5) * mm});
            skLineSegment(sketch, "E55.top", {"start": v(253.33, 88.21) * mm, "end": v(365, 88.21) * mm});
            skLineSegment(sketch, "E55.left", {"start": v(253.33, 9.5) * mm, "end": v(253.33, 88.21) * mm});
            skLineSegment(sketch, "E55.right", {"start": v(365, 9.5) * mm, "end": v(365, 88.21) * mm});
            skSolve(sketch);
        }
        {
            var Q0;
            Q0=makeQuery(id+"F13.imprint","IMPRINT",FACE,{"disambiguationData":[TD([[makeQuery(id+"F13.imprint","IMPRINT",EDGE,{"derivedFrom":sQuery(id+"F13.wireOp",EDGE,"E53.bottom")}),1.0]])]});
            var Q1;
            Q1=makeQuery(id+"F13.imprint","IMPRINT",FACE,{"disambiguationData":[TD([[makeQuery(id+"F13.imprint","IMPRINT",EDGE,{"derivedFrom":sQuery(id+"F13.wireOp",EDGE,"E54.bottom")}),1.0]])]});
            var Q2;
            Q2=makeQuery(id+"F13.imprint","IMPRINT",FACE,{"disambiguationData":[TD([[makeQuery(id+"F13.imprint","IMPRINT",EDGE,{"derivedFrom":sQuery(id+"F13.wireOp",EDGE,"E55.bottom")}),1.0]])]});
            extrude(context, id + "F14", {"entities" : qUnion([Q0, Q1, Q2]), "oppositeDirection" : true, "depth" : 8 * mm, "offsetDistance" : 25 * mm, "hasSecondDirection" : true, "secondDirectionOppositeDirection" : true, "secondDirectionDepth" : 2 * mm});
        }
    });
